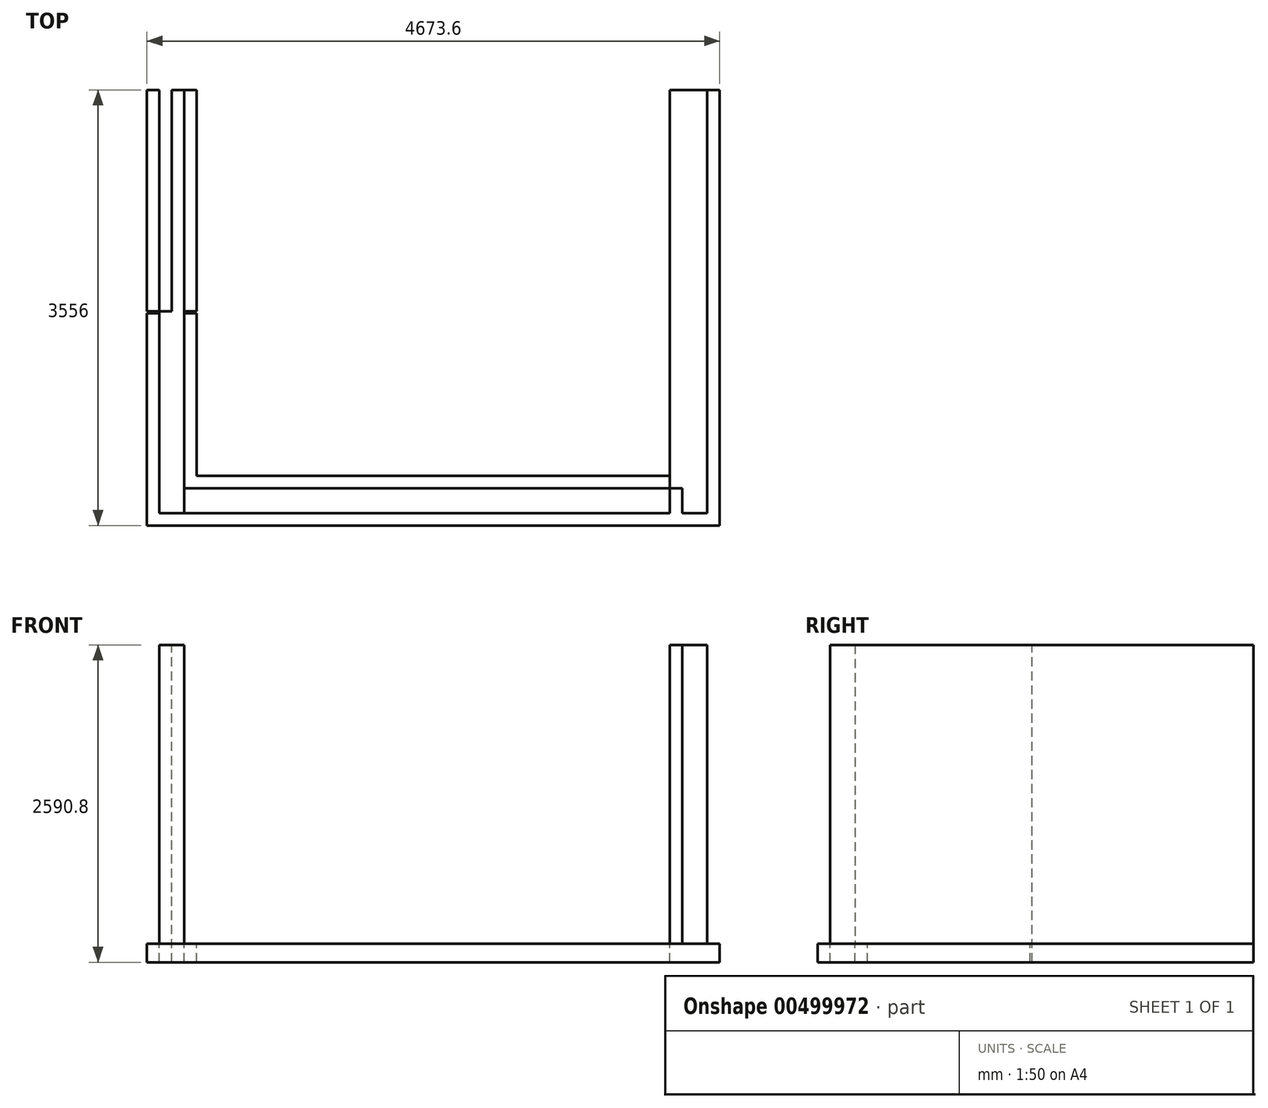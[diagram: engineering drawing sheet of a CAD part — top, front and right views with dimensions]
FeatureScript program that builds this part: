
annotation { "Feature Type Name" : "Feature", "Feature Type Description" : "" }
export const myFeature = defineFeature(function(context is Context, id is Id, definition is map)
    precondition{}
    {
        {
            var Q0;
            Q0=qCreatedBy(makeId("Top.planeOp"),FACE);
            var sketch = newSketch(context, id + "F0", { "sketchPlane" : qUnion([Q0])});
            skLineSegment(sketch, "E0.bottom", {"start": v(-203.2, 1778) * mm, "end": v(203.2, 1778) * mm});
            skLineSegment(sketch, "E0.top", {"start": v(-203.2, -1778) * mm, "end": v(203.2, -1778) * mm});
            skLineSegment(sketch, "E0.left", {"start": v(-203.2, 1778) * mm, "end": v(-203.2, -1778) * mm});
            skLineSegment(sketch, "E0.right", {"start": v(203.2, 1778) * mm, "end": v(203.2, -1778) * mm});
            skPoint(sketch, "E0.middle", {"position": v(0, 0) * mm});
            skLineSegment(sketch, "E1.bottom", {"start": v(203.2, -1778) * mm, "end": v(4064, -1778) * mm});
            skLineSegment(sketch, "E1.top", {"start": v(203.2, -1371.6) * mm, "end": v(4064, -1371.6) * mm});
            skLineSegment(sketch, "E1.left", {"start": v(203.2, -1778) * mm, "end": v(203.2, -1371.6) * mm});
            skLineSegment(sketch, "E1.right", {"start": v(4064, -1778) * mm, "end": v(4064, -1371.6) * mm});
            skLineSegment(sketch, "E2.bottom", {"start": v(4064, -1778) * mm, "end": v(4470.4, -1778) * mm});
            skLineSegment(sketch, "E2.top", {"start": v(4064, 1778) * mm, "end": v(4470.4, 1778) * mm});
            skLineSegment(sketch, "E2.left", {"start": v(4064, -1778) * mm, "end": v(4064, 1778) * mm});
            skLineSegment(sketch, "E2.right", {"start": v(4470.4, -1778) * mm, "end": v(4470.4, 1778) * mm});
            skLineSegment(sketch, "E3.bottom", {"start": v(4165.6, 1778) * mm, "end": v(4368.8, 1778) * mm});
            skLineSegment(sketch, "E3.top", {"start": v(4165.6, -1676.4) * mm, "end": v(4368.8, -1676.4) * mm});
            skLineSegment(sketch, "E3.left", {"start": v(4165.6, 1778) * mm, "end": v(4165.6, -1676.4) * mm});
            skLineSegment(sketch, "E3.right", {"start": v(4368.8, 1778) * mm, "end": v(4368.8, -1676.4) * mm});
            skLineSegment(sketch, "E4.bottom", {"start": v(-101.6, 1778) * mm, "end": v(101.6, 1778) * mm});
            skLineSegment(sketch, "E4.top", {"start": v(-101.6, -1676.4) * mm, "end": v(101.6, -1676.4) * mm});
            skLineSegment(sketch, "E4.left", {"start": v(-101.6, 1778) * mm, "end": v(-101.6, -1676.4) * mm});
            skLineSegment(sketch, "E4.right", {"start": v(101.6, 1778) * mm, "end": v(101.6, -1676.4) * mm});
            skLineSegment(sketch, "E5.bottom", {"start": v(101.6, -1676.4) * mm, "end": v(4165.6, -1676.4) * mm});
            skLineSegment(sketch, "E5.top", {"start": v(101.6, -1473.2) * mm, "end": v(4165.6, -1473.2) * mm});
            skLineSegment(sketch, "E5.left", {"start": v(101.6, -1676.4) * mm, "end": v(101.6, -1473.2) * mm});
            skLineSegment(sketch, "E5.right", {"start": v(4165.6, -1676.4) * mm, "end": v(4165.6, -1473.2) * mm});
            skLineSegment(sketch, "E6", {"start": v(-203.2, -46.89) * mm, "end": v(203.2, -46.89) * mm});
            skLineSegment(sketch, "E7", {"start": v(4267.2, 1778) * mm, "end": v(4267.2, -1676.4) * mm});
            skLineSegment(sketch, "E8", {"start": v(0, 1778) * mm, "end": v(0, -1676.4) * mm});
            skLineSegment(sketch, "E9", {"start": v(0, -1574.8) * mm, "end": v(4165.6, -1574.8) * mm});
            skLineSegment(sketch, "E10", {"start": v(-203.2, -30.77) * mm, "end": v(203.2, -30.77) * mm});
            skSolve(sketch);
        }
        {
            var Q0;
            {var subQ0=sQuery(id+"F0.wireOp",EDGE,"E3.right");Q0=makeQuery(id+"F0.imprint","IMPRINT",FACE,{"disambiguationData":[TD([[makeQuery(id+"F0.imprint","IMPRINT",EDGE,{"derivedFrom":subQ0}),-1.0]])]});}
            var Q1;
            {var subQ0=sQuery(id+"F0.wireOp",EDGE,"E1.bottom");Q1=makeQuery(id+"F0.imprint","IMPRINT",FACE,{"disambiguationData":[TD([[makeQuery(id+"F0.imprint","IMPRINT",EDGE,{"derivedFrom":subQ0}),1.0]])]});}
            var Q2;
            {var subQ0=sQuery(id+"F0.wireOp",EDGE,"E1.top");Q2=makeQuery(id+"F0.imprint","IMPRINT",FACE,{"disambiguationData":[TD([[makeQuery(id+"F0.imprint","IMPRINT",EDGE,{"derivedFrom":subQ0}),-1.0]])]});}
            var Q3;
            {var subQ0=sQuery(id+"F0.wireOp",EDGE,"E3.left");Q3=makeQuery(id+"F0.imprint","IMPRINT",FACE,{"disambiguationData":[TD([[makeQuery(id+"F0.imprint","IMPRINT",EDGE,{"derivedFrom":subQ0}),-1.0]])]});}
            var Q4;
            {var subQ5=sQuery(id+"F0.wireOp",EDGE,"E0.right");var subQ7=sQuery(id+"F0.wireOp",EDGE,"E6");var subQ8=makeQuery(id+"F0.imprint","INTERSECT",VERTEX,{"derivedFrom":[subQ5,subQ7]});Q4=makeQuery(id+"F0.imprint","IMPRINT",FACE,{"disambiguationData":[TD([[makeQuery(id+"F0.imprint","IMPRINT",EDGE,{"disambiguationData":[TD([[subQ8,1.0]])],"derivedFrom":subQ7}),-1.0]])]});}
            var Q5;
            {var subQ2=sQuery(id+"F0.wireOp",EDGE,"E2.bottom");Q5=makeQuery(id+"F0.imprint","IMPRINT",FACE,{"disambiguationData":[TD([[makeQuery(id+"F0.imprint","IMPRINT",EDGE,{"derivedFrom":subQ2}),1.0]])]});}
            var Q6;
            {var subQ5=sQuery(id+"F0.wireOp",EDGE,"E0.top");Q6=makeQuery(id+"F0.imprint","IMPRINT",FACE,{"disambiguationData":[TD([[makeQuery(id+"F0.imprint","IMPRINT",EDGE,{"derivedFrom":subQ5}),1.0]])]});}
            var Q7;
            {var subQ0=sQuery(id+"F0.wireOp",EDGE,"E3.left");Q7=makeQuery(id+"F0.imprint","IMPRINT",FACE,{"disambiguationData":[TD([[makeQuery(id+"F0.imprint","IMPRINT",EDGE,{"derivedFrom":subQ0}),1.0]])]});}
            var Q8;
            {var subQ4=sQuery(id+"F0.wireOp",EDGE,"E4.left");var subQ5=sQuery(id+"F0.wireOp",EDGE,"E4.top");var subQ6=makeQuery(id+"F0.imprint","INTERSECT",VERTEX,{"derivedFrom":[subQ5,subQ4]});Q8=makeQuery(id+"F0.imprint","IMPRINT",FACE,{"disambiguationData":[TD([[makeQuery(id+"F0.imprint","IMPRINT",EDGE,{"disambiguationData":[TD([[subQ6,-1.0]])],"derivedFrom":subQ5}),1.0]])]});}
            var Q9;
            {var subQ3=sQuery(id+"F0.wireOp",EDGE,"E6");var subQ5=sQuery(id+"F0.wireOp",EDGE,"E4.right");var subQ6=makeQuery(id+"F0.imprint","INTERSECT",VERTEX,{"derivedFrom":[subQ5,subQ3]});Q9=makeQuery(id+"F0.imprint","IMPRINT",FACE,{"disambiguationData":[TD([[makeQuery(id+"F0.imprint","IMPRINT",EDGE,{"disambiguationData":[TD([[subQ6,1.0]])],"derivedFrom":subQ3}),-1.0]])]});}
            var Q10;
            {var subQ1=sQuery(id+"F0.wireOp",EDGE,"E4.top");var subQ3=sQuery(id+"F0.wireOp",EDGE,"E8");var subQ4=makeQuery(id+"F0.imprint","INTERSECT",VERTEX,{"derivedFrom":[subQ1,subQ3]});Q10=makeQuery(id+"F0.imprint","IMPRINT",FACE,{"disambiguationData":[TD([[makeQuery(id+"F0.imprint","IMPRINT",EDGE,{"disambiguationData":[TD([[subQ4,1.0]])],"derivedFrom":subQ3}),1.0]])]});}
            var Q11;
            {var subQ0=sQuery(id+"F0.wireOp",EDGE,"E9");var subQ1=sQuery(id+"F0.wireOp",EDGE,"E1.left");var subQ2=makeQuery(id+"F0.imprint","INTERSECT",VERTEX,{"derivedFrom":[subQ1,subQ0]});Q11=makeQuery(id+"F0.imprint","IMPRINT",FACE,{"disambiguationData":[TD([[makeQuery(id+"F0.imprint","IMPRINT",EDGE,{"disambiguationData":[TD([[subQ2,-1.0]])],"derivedFrom":subQ1}),1.0]])]});}
            var Q12;
            {var subQ0=sQuery(id+"F0.wireOp",EDGE,"E5.bottom");var subQ1=sQuery(id+"F0.wireOp",EDGE,"E1.left");var subQ2=makeQuery(id+"F0.imprint","INTERSECT",VERTEX,{"derivedFrom":[subQ1,subQ0]});Q12=makeQuery(id+"F0.imprint","IMPRINT",FACE,{"disambiguationData":[TD([[makeQuery(id+"F0.imprint","IMPRINT",EDGE,{"disambiguationData":[TD([[subQ2,-1.0]])],"derivedFrom":subQ1}),1.0]])]});}
            var Q13;
            {var subQ0=sQuery(id+"F0.wireOp",EDGE,"E9");var subQ1=sQuery(id+"F0.wireOp",EDGE,"E1.left");var subQ2=makeQuery(id+"F0.imprint","INTERSECT",VERTEX,{"derivedFrom":[subQ1,subQ0]});Q13=makeQuery(id+"F0.imprint","IMPRINT",FACE,{"disambiguationData":[TD([[makeQuery(id+"F0.imprint","IMPRINT",EDGE,{"disambiguationData":[TD([[subQ2,-1.0]])],"derivedFrom":subQ1}),-1.0]])]});}
            var Q14;
            {var subQ0=sQuery(id+"F0.wireOp",EDGE,"E5.bottom");var subQ1=sQuery(id+"F0.wireOp",EDGE,"E1.left");var subQ2=makeQuery(id+"F0.imprint","INTERSECT",VERTEX,{"derivedFrom":[subQ1,subQ0]});Q14=makeQuery(id+"F0.imprint","IMPRINT",FACE,{"disambiguationData":[TD([[makeQuery(id+"F0.imprint","IMPRINT",EDGE,{"disambiguationData":[TD([[subQ2,-1.0]])],"derivedFrom":subQ1}),-1.0]])]});}
            var Q15;
            {var subQ0=sQuery(id+"F0.wireOp",EDGE,"E9");var subQ1=sQuery(id+"F0.wireOp",EDGE,"E2.left");var subQ2=makeQuery(id+"F0.imprint","INTERSECT",VERTEX,{"derivedFrom":[subQ1,subQ0]});Q15=makeQuery(id+"F0.imprint","IMPRINT",FACE,{"disambiguationData":[TD([[makeQuery(id+"F0.imprint","IMPRINT",EDGE,{"disambiguationData":[TD([[subQ2,-1.0]])],"derivedFrom":subQ1}),-1.0]])]});}
            var Q16;
            {var subQ0=sQuery(id+"F0.wireOp",EDGE,"E5.bottom");var subQ1=sQuery(id+"F0.wireOp",EDGE,"E2.left");var subQ2=makeQuery(id+"F0.imprint","INTERSECT",VERTEX,{"derivedFrom":[subQ1,subQ0]});Q16=makeQuery(id+"F0.imprint","IMPRINT",FACE,{"disambiguationData":[TD([[makeQuery(id+"F0.imprint","IMPRINT",EDGE,{"disambiguationData":[TD([[subQ2,-1.0]])],"derivedFrom":subQ1}),-1.0]])]});}
            var Q17;
            {var subQ0=sQuery(id+"F0.wireOp",EDGE,"E0.left");var subQ1=sQuery(id+"F0.wireOp",EDGE,"E0.bottom");var subQ2=makeQuery(id+"F0.imprint","INTERSECT",VERTEX,{"derivedFrom":[subQ1,subQ0]});Q17=makeQuery(id+"F0.imprint","IMPRINT",FACE,{"disambiguationData":[TD([[makeQuery(id+"F0.imprint","IMPRINT",EDGE,{"disambiguationData":[TD([[subQ2,-1.0]])],"derivedFrom":subQ0}),1.0]])]});}
            var Q18;
            {var subQ1=sQuery(id+"F0.wireOp",EDGE,"E4.bottom");var subQ3=sQuery(id+"F0.wireOp",EDGE,"E8");var subQ4=makeQuery(id+"F0.imprint","INTERSECT",VERTEX,{"derivedFrom":[subQ1,subQ3]});Q18=makeQuery(id+"F0.imprint","IMPRINT",FACE,{"disambiguationData":[TD([[makeQuery(id+"F0.imprint","IMPRINT",EDGE,{"disambiguationData":[TD([[subQ4,-1.0]])],"derivedFrom":subQ3}),-1.0]])]});}
            var Q19;
            {var subQ1=sQuery(id+"F0.wireOp",EDGE,"E4.bottom");var subQ3=sQuery(id+"F0.wireOp",EDGE,"E8");var subQ4=makeQuery(id+"F0.imprint","INTERSECT",VERTEX,{"derivedFrom":[subQ1,subQ3]});Q19=makeQuery(id+"F0.imprint","IMPRINT",FACE,{"disambiguationData":[TD([[makeQuery(id+"F0.imprint","IMPRINT",EDGE,{"disambiguationData":[TD([[subQ4,-1.0]])],"derivedFrom":subQ3}),1.0]])]});}
            var Q20;
            {var subQ0=sQuery(id+"F0.wireOp",EDGE,"E0.right");var subQ1=sQuery(id+"F0.wireOp",EDGE,"E0.bottom");var subQ2=makeQuery(id+"F0.imprint","INTERSECT",VERTEX,{"derivedFrom":[subQ1,subQ0]});Q20=makeQuery(id+"F0.imprint","IMPRINT",FACE,{"disambiguationData":[TD([[makeQuery(id+"F0.imprint","IMPRINT",EDGE,{"disambiguationData":[TD([[subQ2,-1.0]])],"derivedFrom":subQ0}),-1.0]])]});}
            var Q21;
            {var subQ0=sQuery(id+"F0.wireOp",EDGE,"E10");var subQ1=sQuery(id+"F0.wireOp",EDGE,"E4.left");var subQ2=makeQuery(id+"F0.imprint","INTERSECT",VERTEX,{"derivedFrom":[subQ1,subQ0]});Q21=makeQuery(id+"F0.imprint","IMPRINT",FACE,{"disambiguationData":[TD([[makeQuery(id+"F0.imprint","IMPRINT",EDGE,{"disambiguationData":[TD([[subQ2,-1.0]])],"derivedFrom":subQ1}),1.0]])]});}
            extrude(context, id + "F1", {"entities" : qUnion([Q0, Q1, Q2, Q3, Q4, Q5, Q6, Q7, Q8, Q9, Q10, Q11, Q12, Q13, Q14, Q15, Q16, Q17, Q18, Q19, Q20, Q21]), "oppositeDirection" : true, "depth" : 152.4 * mm, "offsetDistance" : 25.4 * mm});
        }
        {
            var Q0;
            {var subQ4=sQuery(id+"F0.wireOp",EDGE,"E4.left");var subQ5=sQuery(id+"F0.wireOp",EDGE,"E4.top");var subQ6=makeQuery(id+"F0.imprint","INTERSECT",VERTEX,{"derivedFrom":[subQ5,subQ4]});Q0=makeQuery(id+"F0.imprint","IMPRINT",FACE,{"disambiguationData":[TD([[makeQuery(id+"F0.imprint","IMPRINT",EDGE,{"disambiguationData":[TD([[subQ6,-1.0]])],"derivedFrom":subQ5}),1.0]])]});}
            var Q1;
            {var subQ3=sQuery(id+"F0.wireOp",EDGE,"E6");var subQ5=sQuery(id+"F0.wireOp",EDGE,"E4.right");var subQ6=makeQuery(id+"F0.imprint","INTERSECT",VERTEX,{"derivedFrom":[subQ5,subQ3]});Q1=makeQuery(id+"F0.imprint","IMPRINT",FACE,{"disambiguationData":[TD([[makeQuery(id+"F0.imprint","IMPRINT",EDGE,{"disambiguationData":[TD([[subQ6,1.0]])],"derivedFrom":subQ3}),-1.0]])]});}
            var Q2;
            {var subQ1=sQuery(id+"F0.wireOp",EDGE,"E4.top");var subQ3=sQuery(id+"F0.wireOp",EDGE,"E8");var subQ4=makeQuery(id+"F0.imprint","INTERSECT",VERTEX,{"derivedFrom":[subQ1,subQ3]});Q2=makeQuery(id+"F0.imprint","IMPRINT",FACE,{"disambiguationData":[TD([[makeQuery(id+"F0.imprint","IMPRINT",EDGE,{"disambiguationData":[TD([[subQ4,1.0]])],"derivedFrom":subQ3}),1.0]])]});}
            var Q3;
            {var subQ0=sQuery(id+"F0.wireOp",EDGE,"E9");var subQ1=sQuery(id+"F0.wireOp",EDGE,"E1.left");var subQ2=makeQuery(id+"F0.imprint","INTERSECT",VERTEX,{"derivedFrom":[subQ1,subQ0]});Q3=makeQuery(id+"F0.imprint","IMPRINT",FACE,{"disambiguationData":[TD([[makeQuery(id+"F0.imprint","IMPRINT",EDGE,{"disambiguationData":[TD([[subQ2,-1.0]])],"derivedFrom":subQ1}),1.0]])]});}
            var Q4;
            {var subQ0=sQuery(id+"F0.wireOp",EDGE,"E5.bottom");var subQ1=sQuery(id+"F0.wireOp",EDGE,"E1.left");var subQ2=makeQuery(id+"F0.imprint","INTERSECT",VERTEX,{"derivedFrom":[subQ1,subQ0]});Q4=makeQuery(id+"F0.imprint","IMPRINT",FACE,{"disambiguationData":[TD([[makeQuery(id+"F0.imprint","IMPRINT",EDGE,{"disambiguationData":[TD([[subQ2,-1.0]])],"derivedFrom":subQ1}),1.0]])]});}
            var Q5;
            {var subQ0=sQuery(id+"F0.wireOp",EDGE,"E9");var subQ1=sQuery(id+"F0.wireOp",EDGE,"E1.left");var subQ2=makeQuery(id+"F0.imprint","INTERSECT",VERTEX,{"derivedFrom":[subQ1,subQ0]});Q5=makeQuery(id+"F0.imprint","IMPRINT",FACE,{"disambiguationData":[TD([[makeQuery(id+"F0.imprint","IMPRINT",EDGE,{"disambiguationData":[TD([[subQ2,-1.0]])],"derivedFrom":subQ1}),-1.0]])]});}
            var Q6;
            {var subQ0=sQuery(id+"F0.wireOp",EDGE,"E5.bottom");var subQ1=sQuery(id+"F0.wireOp",EDGE,"E1.left");var subQ2=makeQuery(id+"F0.imprint","INTERSECT",VERTEX,{"derivedFrom":[subQ1,subQ0]});Q6=makeQuery(id+"F0.imprint","IMPRINT",FACE,{"disambiguationData":[TD([[makeQuery(id+"F0.imprint","IMPRINT",EDGE,{"disambiguationData":[TD([[subQ2,-1.0]])],"derivedFrom":subQ1}),-1.0]])]});}
            var Q7;
            {var subQ0=sQuery(id+"F0.wireOp",EDGE,"E5.bottom");var subQ1=sQuery(id+"F0.wireOp",EDGE,"E2.left");var subQ2=makeQuery(id+"F0.imprint","INTERSECT",VERTEX,{"derivedFrom":[subQ1,subQ0]});Q7=makeQuery(id+"F0.imprint","IMPRINT",FACE,{"disambiguationData":[TD([[makeQuery(id+"F0.imprint","IMPRINT",EDGE,{"disambiguationData":[TD([[subQ2,-1.0]])],"derivedFrom":subQ1}),-1.0]])]});}
            var Q8;
            {var subQ0=sQuery(id+"F0.wireOp",EDGE,"E9");var subQ1=sQuery(id+"F0.wireOp",EDGE,"E2.left");var subQ2=makeQuery(id+"F0.imprint","INTERSECT",VERTEX,{"derivedFrom":[subQ1,subQ0]});Q8=makeQuery(id+"F0.imprint","IMPRINT",FACE,{"disambiguationData":[TD([[makeQuery(id+"F0.imprint","IMPRINT",EDGE,{"disambiguationData":[TD([[subQ2,-1.0]])],"derivedFrom":subQ1}),-1.0]])]});}
            var Q9;
            {var subQ0=sQuery(id+"F0.wireOp",EDGE,"E3.left");Q9=makeQuery(id+"F0.imprint","IMPRINT",FACE,{"disambiguationData":[TD([[makeQuery(id+"F0.imprint","IMPRINT",EDGE,{"derivedFrom":subQ0}),1.0]])]});}
            var Q10;
            {var subQ0=sQuery(id+"F0.wireOp",EDGE,"E3.right");Q10=makeQuery(id+"F0.imprint","IMPRINT",FACE,{"disambiguationData":[TD([[makeQuery(id+"F0.imprint","IMPRINT",EDGE,{"derivedFrom":subQ0}),-1.0]])]});}
            var Q11;
            {var subQ1=sQuery(id+"F0.wireOp",EDGE,"E4.bottom");var subQ3=sQuery(id+"F0.wireOp",EDGE,"E8");var subQ4=makeQuery(id+"F0.imprint","INTERSECT",VERTEX,{"derivedFrom":[subQ1,subQ3]});Q11=makeQuery(id+"F0.imprint","IMPRINT",FACE,{"disambiguationData":[TD([[makeQuery(id+"F0.imprint","IMPRINT",EDGE,{"disambiguationData":[TD([[subQ4,-1.0]])],"derivedFrom":subQ3}),-1.0]])]});}
            var Q12;
            {var subQ1=sQuery(id+"F0.wireOp",EDGE,"E4.bottom");var subQ3=sQuery(id+"F0.wireOp",EDGE,"E8");var subQ4=makeQuery(id+"F0.imprint","INTERSECT",VERTEX,{"derivedFrom":[subQ1,subQ3]});Q12=makeQuery(id+"F0.imprint","IMPRINT",FACE,{"disambiguationData":[TD([[makeQuery(id+"F0.imprint","IMPRINT",EDGE,{"disambiguationData":[TD([[subQ4,-1.0]])],"derivedFrom":subQ3}),1.0]])]});}
            var Q13;
            {var subQ0=sQuery(id+"F0.wireOp",EDGE,"E10");var subQ1=sQuery(id+"F0.wireOp",EDGE,"E4.left");var subQ2=makeQuery(id+"F0.imprint","INTERSECT",VERTEX,{"derivedFrom":[subQ1,subQ0]});Q13=makeQuery(id+"F0.imprint","IMPRINT",FACE,{"disambiguationData":[TD([[makeQuery(id+"F0.imprint","IMPRINT",EDGE,{"disambiguationData":[TD([[subQ2,-1.0]])],"derivedFrom":subQ1}),1.0]])]});}
            extrude(context, id + "F2", {"entities" : qUnion([Q0, Q1, Q2, Q3, Q4, Q5, Q6, Q7, Q8, Q9, Q10, Q11, Q12, Q13]), "operationType" : NewBodyOperationType.ADD, "depth" : 2438.4 * mm, "offsetDistance" : 25.4 * mm});
        }
    });
